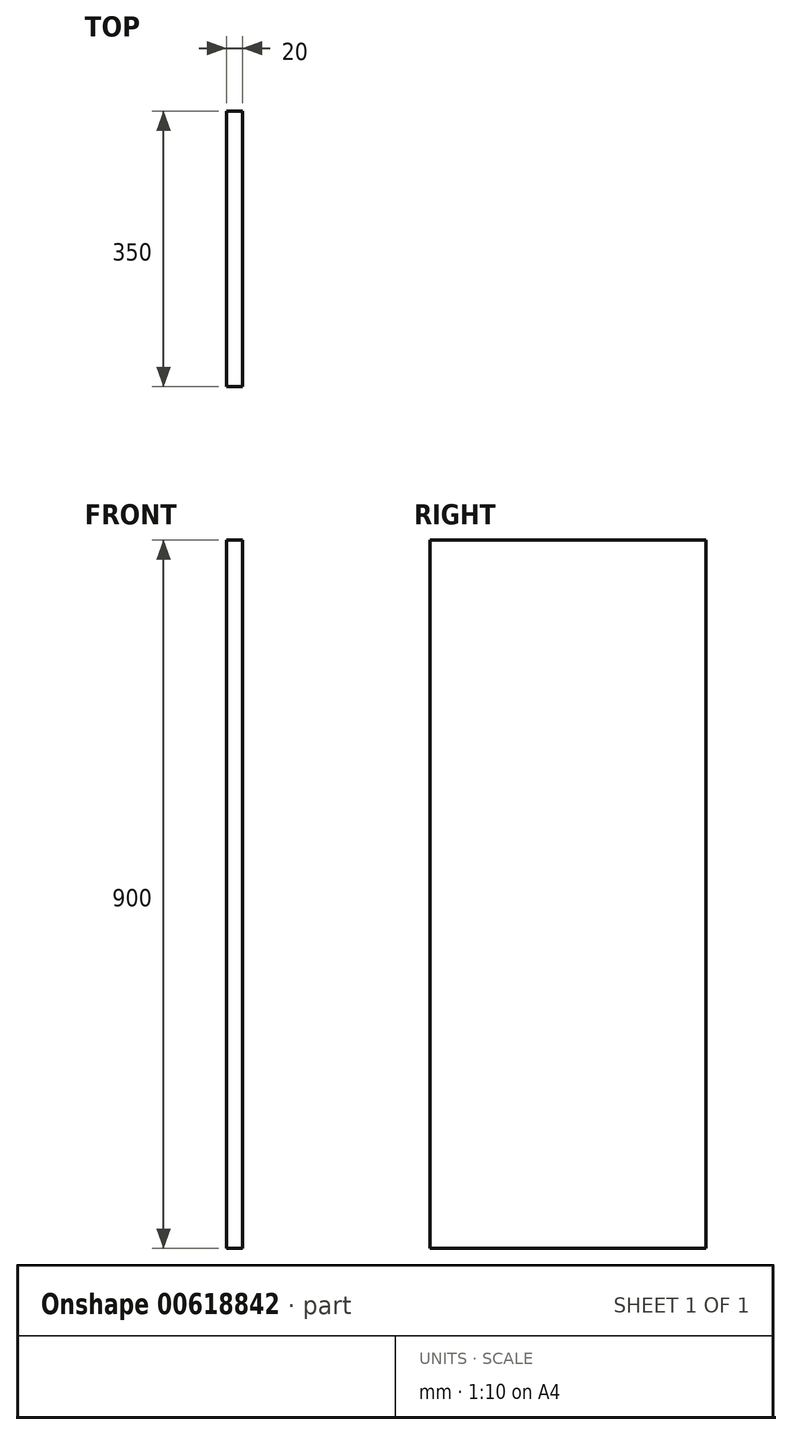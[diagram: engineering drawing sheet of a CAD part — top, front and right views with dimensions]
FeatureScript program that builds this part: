
annotation { "Feature Type Name" : "Feature", "Feature Type Description" : "" }
export const myFeature = defineFeature(function(context is Context, id is Id, definition is map)
    precondition{}
    {
        {
            var Q0;
            Q0=qCreatedBy(makeId("Right.planeOp"),FACE);
            var sketch = newSketch(context, id + "F0", { "sketchPlane" : qUnion([Q0])});
            skLineSegment(sketch, "E0.bottom", {"start": v(-175, 450) * mm, "end": v(175, 450) * mm});
            skLineSegment(sketch, "E0.top", {"start": v(-175, -450) * mm, "end": v(175, -450) * mm});
            skLineSegment(sketch, "E0.left", {"start": v(-175, 450) * mm, "end": v(-175, -450) * mm});
            skLineSegment(sketch, "E0.right", {"start": v(175, 450) * mm, "end": v(175, -450) * mm});
            skPoint(sketch, "E0.middle", {"position": v(0, 0) * mm});
            skSolve(sketch);
        }
        {
            var Q0;
            Q0 = qSketchRegion(id + "F0", true);
            extrude(context, id + "F1", {"entities" : qUnion([Q0]), "depth" : 20 * mm, "offsetDistance" : 25 * mm});
        }
    });
